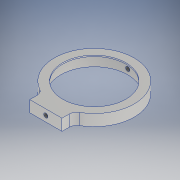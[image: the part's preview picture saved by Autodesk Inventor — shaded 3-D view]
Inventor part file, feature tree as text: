
AUTODESK INVENTOR PART (.ipt)
format: ipt  version: 2017 SP1 (Build 210196100, 196)  size: 181,248 bytes
history: native  units: mm
features: fillet x6, sketch x5, extrude x3, hole x2, plane x1
ambient origin geometry x8: Origin, YZ Plane, XZ Plane, XY Plane, X Axis, Y Axis, Z Axis, Center Point
bodies: Solid1 (feature_tree)
feature tree (17):
  extrude  "Extrusion1"  Depth=6.0mm
  fillet  "Fillet1"  Radius=62.8mm
  fillet  "Fillet2"  Radius=8.726646mm
  fillet  "Fillet3"  Radius=8.0mm
  fillet  "Fillet4"  Radius=6.0mm
  extrude  "Extrusion2"  Depth=6.0mm
  plane  "Work Plane1"
  hole  "Hole1"  [1 undecoded]
  extrude  "Extrusion3"  Depth=4.0mm
  fillet  "Fillet5"  Radius=38.1mm
  fillet  "Fillet6"  Radius=25.4mm
  hole  "Hole2"  [1 undecoded]
  sketch  "Sketch1"  dims[d0=50.8mm d1=52.8mm d2=62.8mm d4=8.726646mm d5=8.0mm d6=0.0mm d7=6.0mm]
  sketch  "Sketch2"  dims[d8=6.0mm d9=6.0mm]
  sketch  "Sketch3"  dims[d10=6.0mm d11=49.8mm]
  sketch  "Sketch4"  dims[d12=1.0mm d13=0.0mm d14=4.0mm]
  sketch  "Sketch5"  dims[d15=3.302mm d16=8.331mm d17=4.0mm d18=2.0mm d19=90.0deg d20=12.3mm d21=20.594885mm d22=38.1mm d23=25.4mm d24=9.0mm d25=0.0mm d26=6.0mm d27=6.0mm d28=3.242mm d29=8.0mm d30=4.0mm d31=2.0mm d32=90.0deg d33=13.0mm d34=20.594885mm]
note: 2 required parameter values undecoded (feature->parameter linkage not recoverable at this tier; creation-order binding heuristic only, values carry confidence <= 0.55)
